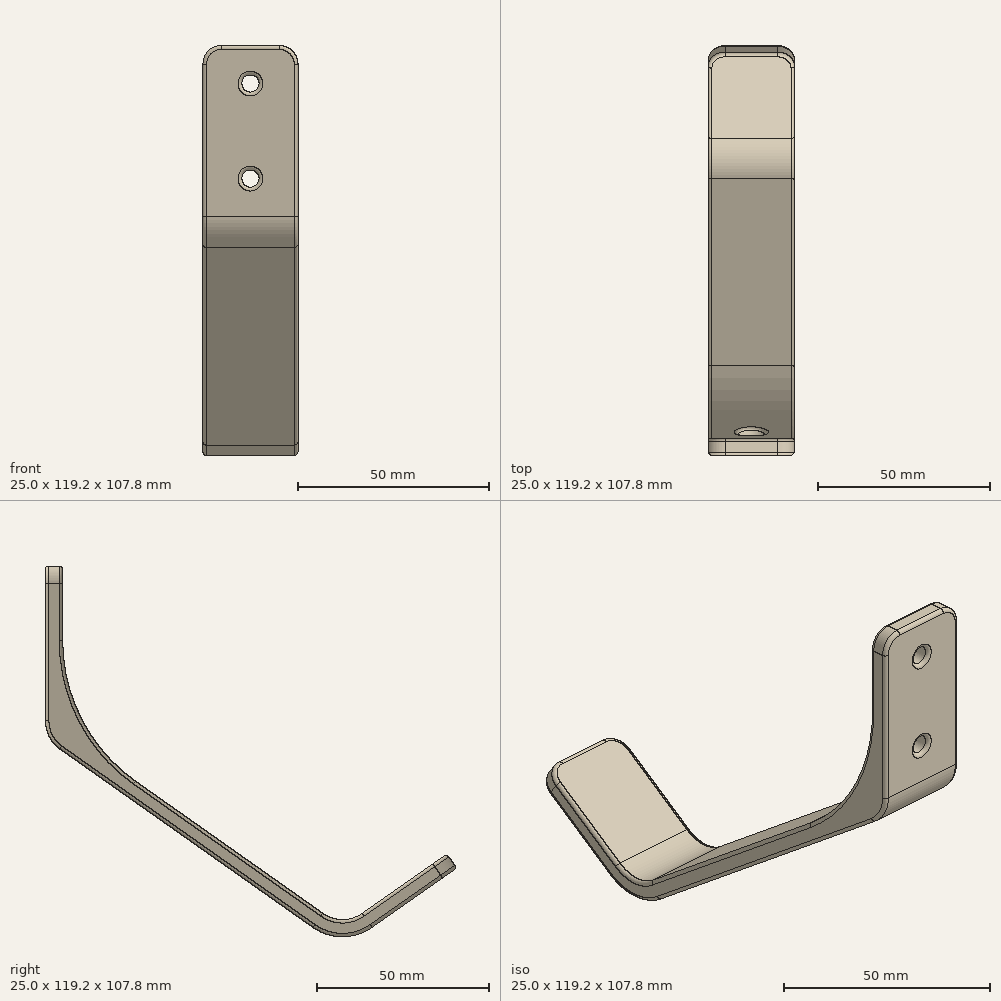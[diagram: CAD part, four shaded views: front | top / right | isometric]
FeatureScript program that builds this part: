
annotation { "Feature Type Name" : "Feature", "Feature Type Description" : "" }
export const myFeature = defineFeature(function(context is Context, id is Id, definition is map)
    precondition{}
    {
        {
            var Q0;
            Q0=qCreatedBy(makeId("Right.planeOp"),FACE);
            var sketch = newSketch(context, id + "F0", { "sketchPlane" : qUnion([Q0])});
            skLineSegment(sketch, "E0", {"start": v(0, 105) * mm, "end": v(0, 60) * mm});
            skLineSegment(sketch, "E1", {"start": v(2.12, 55.91) * mm, "end": v(75.67, 4.05) * mm});
            skLineSegment(sketch, "E2", {"start": v(87.17, 4.03) * mm, "end": v(111.74, 21.24) * mm});
            skPoint(sketch, "E3.visualSharp", {"position": v(81.41, 0) * mm});
            skArc(sketch, "E3.filletArc", {"start": v(75.67, 4.05) * mm, "mid": v(81.42, 2.22) * mm, "end": v(87.17, 4.03) * mm});
            skPoint(sketch, "E4.visualSharp", {"position": v(0, 57.4) * mm});
            skArc(sketch, "E4.filletArc", {"start": v(0, 60) * mm, "mid": v(0.56, 57.7) * mm, "end": v(2.12, 55.91) * mm});
            skLineSegment(sketch, "E5.0", {"start": v(90.04, -0.07) * mm, "end": v(114.61, 17.14) * mm});
            skLineSegment(sketch, "E5.1", {"start": v(-5, 105) * mm, "end": v(-5, 60) * mm});
            skArc(sketch, "E5.2", {"start": v(-5, 60) * mm, "mid": v(-3.88, 55.4) * mm, "end": v(-0.76, 51.83) * mm});
            skLineSegment(sketch, "E5.3", {"start": v(-0.76, 51.83) * mm, "end": v(72.8, -0.04) * mm});
            skArc(sketch, "E5.4", {"start": v(72.8, -0.04) * mm, "mid": v(81.4, -2.78) * mm, "end": v(90.04, -0.07) * mm});
            skLineSegment(sketch, "E6", {"start": v(0, 105) * mm, "end": v(-5, 105) * mm});
            skLineSegment(sketch, "E7", {"start": v(111.74, 21.24) * mm, "end": v(114.61, 17.14) * mm});
            skCircle(sketch, "E8", {"center": v(50, 83.33) * mm, "radius": 50 * mm});
            skSolve(sketch);
        }
        {
            var Q0;
            Q0=makeQuery(id+"F0.imprint","IMPRINT",FACE,{"disambiguationData":[TD([[makeQuery(id+"F0.imprint","IMPRINT",EDGE,{"derivedFrom":sQuery(id+"F0.wireOp",EDGE,"E0")}),-1.0]])]});
            var Q1;
            {var subQ0=sQuery(id+"F0.wireOp",EDGE,"E4.filletArc");Q1=makeQuery(id+"F0.imprint","IMPRINT",FACE,{"disambiguationData":[TD([[makeQuery(id+"F0.imprint","IMPRINT",EDGE,{"derivedFrom":subQ0}),1.0]])]});}
            extrude(context, id + "F1", {"entities" : qUnion([Q0, Q1]), "depth" : 25 * mm, "symmetric" : true});
        }
        {
            var Q0;
            Q0=qCreatedBy(makeId("Front.planeOp"),FACE);
            var sketch = newSketch(context, id + "F2", { "sketchPlane" : qUnion([Q0])});
            skCircle(sketch, "E9", {"center": v(0, 95) * mm, "radius": 2.25 * mm});
            skCircle(sketch, "E10", {"center": v(0, 70) * mm, "radius": 2.25 * mm});
            skCircle(sketch, "E11", {"center": v(0, 70) * mm, "radius": 4 * mm});
            skSolve(sketch);
        }
        {
            var Q0;
            Q0=makeQuery(id+"F2.imprint","IMPRINT",FACE,{"disambiguationData":[TD([[makeQuery(id+"F2.imprint","IMPRINT",EDGE,{"derivedFrom":sQuery(id+"F2.wireOp",EDGE,"E9")}),1.0]])]});
            var Q1;
            Q1=makeQuery(id+"F2.imprint","IMPRINT",FACE,{"disambiguationData":[TD([[makeQuery(id+"F2.imprint","IMPRINT",EDGE,{"derivedFrom":sQuery(id+"F2.wireOp",EDGE,"E10")}),1.0]])]});
            extrude(context, id + "F3", {"entities" : qUnion([Q0, Q1]), "operationType" : NewBodyOperationType.REMOVE, "oppositeDirection" : true, "depth" : 25 * mm, "symmetric" : true});
        }
        {
            var Q0;
            Q0=qSketchRegion(id+"F2",true);
            extrude(context, id + "F4", {"entities" : qUnion([Q0]), "operationType" : NewBodyOperationType.REMOVE, "oppositeDirection" : true, "depth" : 25 * mm});
        }
        {
            var Q0;
            Q0=makeQuery(id+"F1.opExtrude","CAP_EDGE",EDGE,{"disambiguationData":[OSD([sQuery(id+"F0.wireOp",EDGE,"E6")])],"isStart":false});
            var Q1;
            Q1=makeQuery(id+"F1.opExtrude","CAP_EDGE",EDGE,{"disambiguationData":[OSD([sQuery(id+"F0.wireOp",EDGE,"E6")])],"isStart":true});
            var Q2;
            Q2=makeQuery(id+"F1.opExtrude","CAP_EDGE",EDGE,{"disambiguationData":[OSD([sQuery(id+"F0.wireOp",EDGE,"E7")])],"isStart":false});
            var Q3;
            Q3=makeQuery(id+"F1.opExtrude","CAP_EDGE",EDGE,{"disambiguationData":[OSD([sQuery(id+"F0.wireOp",EDGE,"E7")])],"isStart":true});
            fillet(context, id + "F5", {"entities" : qUnion([Q0, Q1, Q2, Q3]), "radius" : 5 * mm, "tangentPropagation" : true, "allowEdgeOverflow" : false});
        }
        {
            var Q0;
            Q0=makeQuery(id+"F1.opExtrude","SWEPT_FACE",FACE,{"disambiguationData":[OSD([sQuery(id+"F0.wireOp",EDGE,"E1")])]});
            var Q1;
            Q1=makeQuery(id+"F1.opExtrude","SWEPT_FACE",FACE,{"disambiguationData":[OSD([sQuery(id+"F0.wireOp",EDGE,"E5.1")])]});
            var Q2;
            Q2=makeQuery(id+"F3.boolean.opBoolean","INTERSECT",EDGE,{"derivedFrom":[makeQuery(id+"F1.opExtrude","SWEPT_FACE",FACE,{"disambiguationData":[OSD([sQuery(id+"F0.wireOp",EDGE,"E0")])]}),makeQuery(id+"F3.opExtrude","SWEPT_FACE",FACE,{"disambiguationData":[OSD([sQuery(id+"F2.wireOp",EDGE,"E9")])]})]});
            var Q3;
            Q3=makeQuery(id+"F4.boolean.opBoolean","INTERSECT",EDGE,{"derivedFrom":[makeQuery(id+"F1.opExtrude","SWEPT_FACE",FACE,{"disambiguationData":[OSD([sQuery(id+"F0.wireOp",EDGE,"E8")])]}),makeQuery(id+"F4.opExtrude","SWEPT_FACE",FACE,{"disambiguationData":[OSD([sQuery(id+"F2.wireOp",EDGE,"E11")])]})]});
            fillet(context, id + "F6", {"entities" : qUnion([Q0, Q1, Q2, Q3]), "radius" : 1 * mm, "tangentPropagation" : true, "allowEdgeOverflow" : false});
        }
    });
